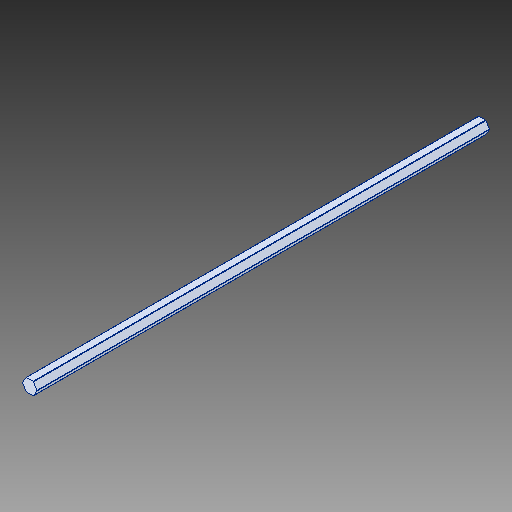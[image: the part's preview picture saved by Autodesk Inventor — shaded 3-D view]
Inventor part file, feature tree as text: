
AUTODESK INVENTOR PART (.ipt)
format: ipt  version: 2017 (Build 210142000, 142)  size: 98,816 bytes
history: native  units: in
note: dims shown in document units (in); Inventor stores cm internally (conversion verified against a paired STEP export)
features: fillet x1
ambient origin geometry x8: Origin, YZ Plane, XZ Plane, XY Plane, X Axis, Y Axis, Z Axis, Center Point
bodies: Solid1 (feature_tree)
feature tree (1):
  fillet  "Fillet1"  [1 undecoded]
note: 1 required parameter value undecoded (feature->parameter linkage not recoverable at this tier; creation-order binding heuristic only, values carry confidence <= 0.55)
